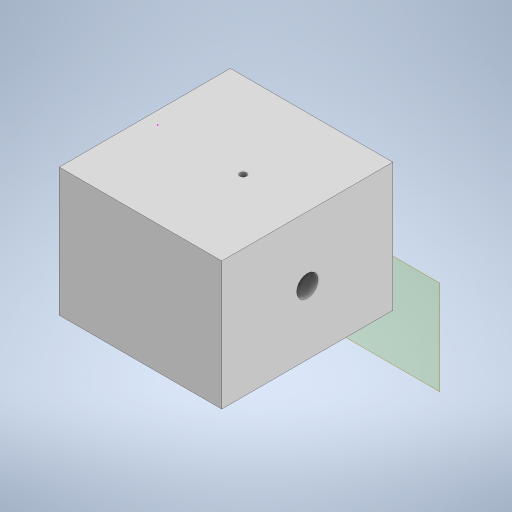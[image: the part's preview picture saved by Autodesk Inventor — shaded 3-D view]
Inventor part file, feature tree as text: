
AUTODESK INVENTOR PART (.ipt)
format: ipt  version: 2023 (Build 270158000, 158)  size: 278,016 bytes
history: native  units: mm
features: sketch x8, plane x6, extrude x6
ambient origin geometry x8: Origin, YZ Plane, XZ Plane, XY Plane, X Axis, Y Axis, Z Axis, Center Point
bodies: Body1 (feature_tree)
feature tree (20):
  plane  "Work Plane13"
  extrude  "Extrusion34"  Depth=40.0mm
  sketch  "Sketch46"  dims[d144=30.0mm d145=0.0mm d146=36.0mm]
  plane  "Work Plane11"
  extrude  "Extrusion35"  Depth=36.0mm
  sketch  "Sketch48"  dims[d150=0.0mm d151=0.0mm d156=20.0mm]
  extrude  "Extrusion36"  Depth=1.5mm
  plane  "Work Plane7"
  extrude  "Extrusion38"  Depth=20.0mm
  plane  "Work Plane4"
  extrude  "Extrusion39"  Depth=15.0mm TaperAngle=0.0deg
  plane  "Work Plane1"
  plane  "Work Plane6"
  extrude  "Extrusion42"  Depth=4.0mm
  sketch  "Sketch45"  dims[d142=38.0mm d143=40.0mm]
  sketch  "Sketch47"  dims[d147=30.0mm d148=-2.617994mm d149=1.5mm]
  sketch  "Sketch49"  dims[d157=15.0mm d158=15.0mm d159=0.0mm]
  sketch  "Sketch58"  dims[d160=4.0mm d161=20.0mm]
  sketch  "Sketch59"  dims[d162=35.0mm d163=0.0mm]
  sketch  "Sketch62"  dims[d172=5.0mm d173=0.0mm d174=0.0mm d49=0.5mm d50=0.872665mm d51=0.5mm d52=0.872665mm d130=0.5mm d131=0.872665mm d132=0.5mm d133=0.872665mm]
